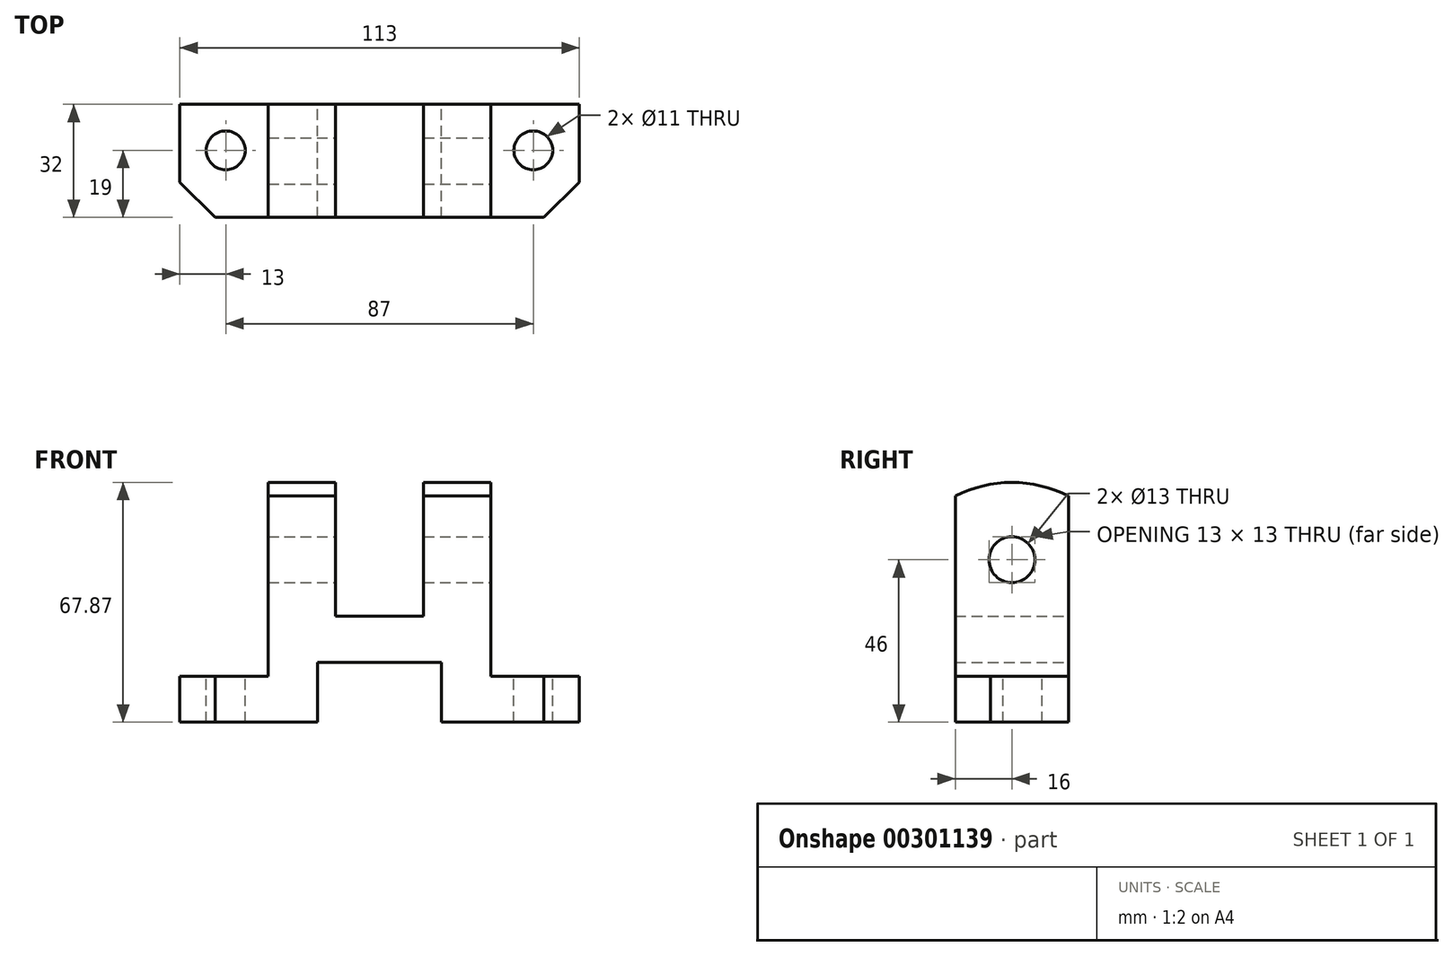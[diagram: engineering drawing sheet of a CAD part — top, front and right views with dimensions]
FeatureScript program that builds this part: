
annotation { "Feature Type Name" : "Feature", "Feature Type Description" : "" }
export const myFeature = defineFeature(function(context is Context, id is Id, definition is map)
    precondition{}
    {
        {
            var Q0;
            Q0=qCreatedBy(makeId("Front.planeOp"),FACE);
            var sketch = newSketch(context, id + "F0", { "sketchPlane" : qUnion([Q0])});
            skLineSegment(sketch, "E0", {"start": v(0, 0) * mm, "end": v(0, 13) * mm});
            skLineSegment(sketch, "E1", {"start": v(0, 13) * mm, "end": v(25, 13) * mm});
            skLineSegment(sketch, "E2", {"start": v(25, 13) * mm, "end": v(25, 64) * mm});
            skLineSegment(sketch, "E3", {"start": v(25, 64) * mm, "end": v(44, 64) * mm});
            skLineSegment(sketch, "E4", {"start": v(44, 64) * mm, "end": v(44, 30) * mm});
            skLineSegment(sketch, "E5", {"start": v(44, 30) * mm, "end": v(69, 30) * mm});
            skLineSegment(sketch, "E6", {"start": v(69, 30) * mm, "end": v(69, 64) * mm});
            skLineSegment(sketch, "E7", {"start": v(69, 64) * mm, "end": v(88, 64) * mm});
            skLineSegment(sketch, "E8", {"start": v(88, 64) * mm, "end": v(88, 13) * mm});
            skLineSegment(sketch, "E9", {"start": v(88, 13) * mm, "end": v(113, 13) * mm});
            skLineSegment(sketch, "E10", {"start": v(113, 13) * mm, "end": v(113, 0) * mm});
            skLineSegment(sketch, "E11", {"start": v(113, 0) * mm, "end": v(74, 0) * mm});
            skLineSegment(sketch, "E12", {"start": v(74, 0) * mm, "end": v(74, 17) * mm});
            skLineSegment(sketch, "E13", {"start": v(74, 17) * mm, "end": v(39, 17) * mm});
            skLineSegment(sketch, "E14", {"start": v(39, 17) * mm, "end": v(39, 0) * mm});
            skLineSegment(sketch, "E15", {"start": v(39, 0) * mm, "end": v(0, 0) * mm});
            skSolve(sketch);
        }
        {
            var Q0;
            Q0=makeQuery(id+"F0.imprint","IMPRINT",FACE,{"disambiguationData":[TD([[makeQuery(id+"F0.imprint","IMPRINT",EDGE,{"derivedFrom":sQuery(id+"F0.wireOp",EDGE,"E0")}),-1.0]])]});
            extrude(context, id + "F1", {"entities" : qUnion([Q0]), "depth" : 32 * mm});
        }
        {
            var Q0;
            Q0=makeQuery(id+"F1.opExtrude","SWEPT_FACE",FACE,{"disambiguationData":[OSD([sQuery(id+"F0.wireOp",EDGE,"E1")])]});
            var sketch = newSketch(context, id + "F2", { "sketchPlane" : qUnion([Q0])});
            skCircle(sketch, "E16", {"center": v(13, -13) * mm, "radius": 5.5 * mm});
            skLineSegment(sketch, "E17", {"start": v(0, -32) * mm, "end": v(0, -22) * mm});
            skLineSegment(sketch, "E18", {"start": v(0, -22) * mm, "end": v(10, -32) * mm});
            skLineSegment(sketch, "E19", {"start": v(10, -32) * mm, "end": v(0, -32) * mm});
            skSolve(sketch);
        }
        {
            var Q0;
            Q0=makeQuery(id+"F2.imprint","IMPRINT",FACE,{"disambiguationData":[TD([[makeQuery(id+"F2.imprint","IMPRINT",EDGE,{"derivedFrom":sQuery(id+"F2.wireOp",EDGE,"E17")}),-1.0]])]});
            var Q1;
            Q1=makeQuery(id+"F2.imprint","IMPRINT",FACE,{"disambiguationData":[TD([[makeQuery(id+"F2.imprint","IMPRINT",EDGE,{"derivedFrom":sQuery(id+"F2.wireOp",EDGE,"E16")}),1.0]])]});
            extrude(context, id + "F3", {"entities" : qUnion([Q0, Q1]), "operationType" : NewBodyOperationType.REMOVE, "endBound" : BoundingType.THROUGH_ALL, "oppositeDirection" : true, "depth" : 25 * mm});
        }
        {
            var Q0;
            Q0=makeQuery(id+"F1.opExtrude","SWEPT_FACE",FACE,{"disambiguationData":[OSD([sQuery(id+"F0.wireOp",EDGE,"E9")])]});
            var sketch = newSketch(context, id + "F4", { "sketchPlane" : qUnion([Q0])});
            skCircle(sketch, "E20", {"center": v(100, -13) * mm, "radius": 5.5 * mm});
            skLineSegment(sketch, "E21", {"start": v(113, -32) * mm, "end": v(113, -22) * mm});
            skLineSegment(sketch, "E22", {"start": v(113, -22) * mm, "end": v(103, -32) * mm});
            skLineSegment(sketch, "E23", {"start": v(103, -32) * mm, "end": v(113, -32) * mm});
            skSolve(sketch);
        }
        {
            var Q0;
            Q0=makeQuery(id+"F4.imprint","IMPRINT",FACE,{"disambiguationData":[TD([[makeQuery(id+"F4.imprint","IMPRINT",EDGE,{"derivedFrom":sQuery(id+"F4.wireOp",EDGE,"E20")}),1.0]])]});
            var Q1;
            Q1=makeQuery(id+"F4.imprint","IMPRINT",FACE,{"disambiguationData":[TD([[makeQuery(id+"F4.imprint","IMPRINT",EDGE,{"derivedFrom":sQuery(id+"F4.wireOp",EDGE,"E21")}),1.0]])]});
            extrude(context, id + "F5", {"entities" : qUnion([Q0, Q1]), "operationType" : NewBodyOperationType.REMOVE, "endBound" : BoundingType.THROUGH_ALL, "oppositeDirection" : true, "depth" : 25 * mm});
        }
        {
            var Q0;
            Q0=makeQuery(id+"F1.opExtrude","SWEPT_FACE",FACE,{"disambiguationData":[OSD([sQuery(id+"F0.wireOp",EDGE,"E4")])]});
            var sketch = newSketch(context, id + "F6", { "sketchPlane" : qUnion([Q0])});
            skArc(sketch, "E24", {"start": v(0, 64) * mm, "mid": v(-16, 67.87) * mm, "end": v(-32, 64) * mm});
            skLineSegment(sketch, "E25", {"start": v(0, 64) * mm, "end": v(-32, 64) * mm});
            skSolve(sketch);
        }
        {
            var Q0;
            Q0=makeQuery(id+"F6.imprint","IMPRINT",FACE,{"disambiguationData":[TD([[makeQuery(id+"F6.imprint","IMPRINT",EDGE,{"derivedFrom":sQuery(id+"F6.wireOp",EDGE,"E24")}),1.0]])]});
            extrude(context, id + "F7", {"entities" : qUnion([Q0]), "operationType" : NewBodyOperationType.ADD, "oppositeDirection" : true, "depth" : 19 * mm});
        }
        {
            var Q0;
            Q0=makeQuery(id+"F1.opExtrude","SWEPT_FACE",FACE,{"disambiguationData":[OSD([sQuery(id+"F0.wireOp",EDGE,"E8")])]});
            var sketch = newSketch(context, id + "F8", { "sketchPlane" : qUnion([Q0])});
            skArc(sketch, "E26", {"start": v(0, 64) * mm, "mid": v(-16, 67.87) * mm, "end": v(-32, 64) * mm});
            skLineSegment(sketch, "E27", {"start": v(0, 64) * mm, "end": v(-32, 64) * mm});
            skSolve(sketch);
        }
        {
            var Q0;
            Q0=makeQuery(id+"F8.imprint","IMPRINT",FACE,{"disambiguationData":[TD([[makeQuery(id+"F8.imprint","IMPRINT",EDGE,{"derivedFrom":sQuery(id+"F8.wireOp",EDGE,"E26")}),1.0]])]});
            extrude(context, id + "F9", {"entities" : qUnion([Q0]), "operationType" : NewBodyOperationType.ADD, "oppositeDirection" : true, "depth" : 19 * mm});
        }
        {
            var Q0;
            Q0=makeQuery(id+"F9.boolean.opBoolean","MERGE",FACE,{"derivedFrom":[makeQuery(id+"F1.opExtrude","SWEPT_FACE",FACE,{"disambiguationData":[OSD([sQuery(id+"F0.wireOp",EDGE,"E8")])]}),makeQuery(id+"F9.opExtrude","CAP_FACE",FACE,{"disambiguationData":[OSD([sQuery(id+"F8.wireOp",EDGE,"E26"),sQuery(id+"F8.wireOp",EDGE,"E27")])],"isStart":true})]});
            var sketch = newSketch(context, id + "F10", { "sketchPlane" : qUnion([Q0])});
            skCircle(sketch, "E28", {"center": v(-16, 46) * mm, "radius": 6.5 * mm});
            skSolve(sketch);
        }
        {
            var Q0;
            Q0=makeQuery(id+"F10.imprint","IMPRINT",FACE,{"disambiguationData":[TD([[makeQuery(id+"F10.imprint","IMPRINT",EDGE,{"derivedFrom":sQuery(id+"F10.wireOp",EDGE,"E28")}),1.0]])]});
            var Q1;
            Q1=sQuery(id+"F10.wireOp",EDGE,"E28");
            extrude(context, id + "F11", {"entities" : qUnion([Q0]), "operationType" : NewBodyOperationType.REMOVE, "surfaceEntities" : qUnion([Q1]), "endBound" : BoundingType.THROUGH_ALL, "oppositeDirection" : true, "depth" : 25 * mm});
        }
    });
